# Revit family: Door_Rollup_SuperSeal_8500Diamond
name_source: partatom
category: Doors
revit_build: Autodesk Revit Architecture 2012 (Build: 20110309_2315(x64)
units: mm (PartAtom-declared; Revit-internal decimal feet)

## types (1)
- ByType
    ADA Compliant = Yes
    Construction Details = http://arcat.com
    Control Box Material = Metal - Stainless Steel - Super Seal - Brushed
    Description = Super Seal
    Expected Lifespan (Years) = 0
    Fire Rating = As Specified
    Frame Finish = Metal - Steel - Super Seal - Painted - Black
    Frame Thickness = 0' - 8"
    Function = Interior
    Height = 9' - 2 1/2"
    Keynote = 08300
    Maintenance Schedule (Months) = 0
    Manual Crank = No
    Manufacturer = Super-Seal Mfg. Ltd
    Manufacturer Fax = 905-850-4440
    Manufacturer Website = http://www.supersealmfg.com
    Max Door Height = 18' - 0"
    Max Door Width = 16' - 0"
    Model = As Specified
    Panel Material = Fabric - Vinyl - Super Seal - Blue
    Product Data = http://arcat.com
    RO Offset = 0' - 0 1/2"
    R_Value = 0
    Rough Height = 9' - 3"
    Rough Width = 9' - 1"
    Sales Information = http://www.supersealmfg.com
    Send Message = http://www.arcat.com &mf=
    Sound Transmission Class (STC) = 0
    Thickness = 0' - 0"
    URL = http://www.supersealmfg.com
    Vision Panel Material = Fabric - Vinyl - Super Seal - Transparent
    Wall Closure = By host
    Warranty Duration (Years) = 0
    Width = 9' - 0"

## geometry (parser evidence)
native form markers: Blend x16, Sweep x12
no freeform markers — native parametric forms only
